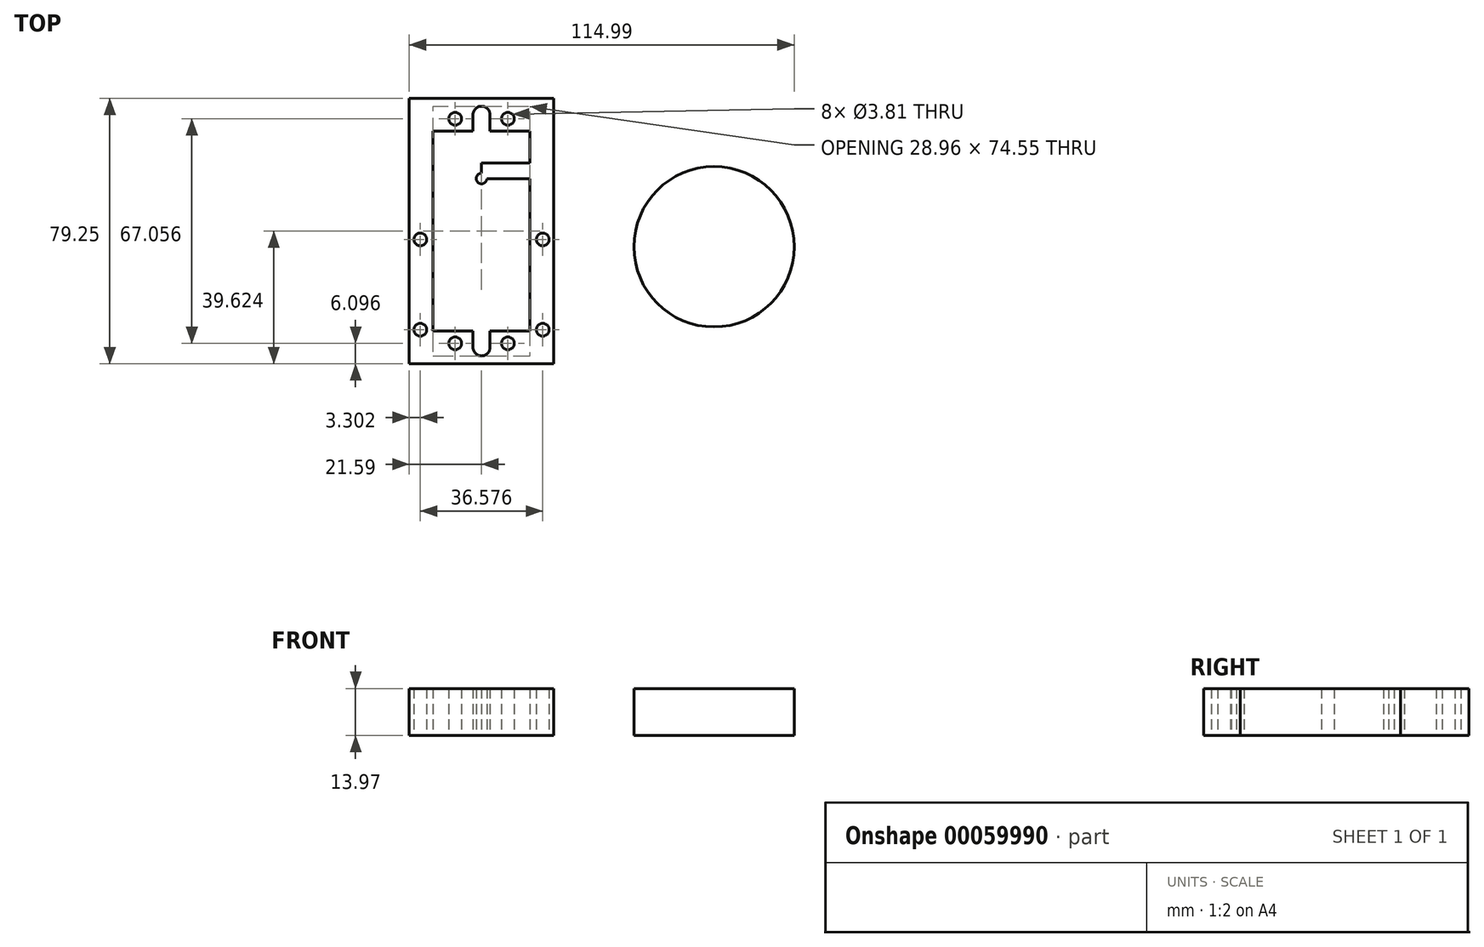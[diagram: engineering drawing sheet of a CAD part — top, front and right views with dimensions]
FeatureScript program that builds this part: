
annotation { "Feature Type Name" : "Feature", "Feature Type Description" : "" }
export const myFeature = defineFeature(function(context is Context, id is Id, definition is map)
    precondition{}
    {
        {
            var Q0;
            Q0=qCreatedBy(makeId("Top.planeOp"),FACE);
            var sketch = newSketch(context, id + "F0", { "sketchPlane" : qUnion([Q0])});
            skLineSegment(sketch, "E0.bottom", {"start": v(0, 0) * mm, "end": v(-43.18, 0) * mm});
            skLineSegment(sketch, "E0.top", {"start": v(0, 79.25) * mm, "end": v(-43.18, 79.25) * mm});
            skLineSegment(sketch, "E0.left", {"start": v(0, 0) * mm, "end": v(0, 79.25) * mm});
            skLineSegment(sketch, "E0.right", {"start": v(-43.18, 0) * mm, "end": v(-43.18, 79.25) * mm});
            skCircle(sketch, "E1", {"center": v(-29.46, 73.15) * mm, "radius": 1.9 * mm});
            skCircle(sketch, "E2", {"center": v(-29.46, 6.1) * mm, "radius": 1.9 * mm});
            skCircle(sketch, "E3", {"center": v(-39.88, 10.16) * mm, "radius": 1.9 * mm});
            skCircle(sketch, "E4", {"center": v(-39.88, 37.1) * mm, "radius": 1.9 * mm});
            skLineSegment(sketch, "E5", {"start": v(-21.59, 0) * mm, "end": v(-21.59, 79.25) * mm, "construction": true});
            skLineSegment(sketch, "E6.bottom", {"start": v(-24.13, 69.47) * mm, "end": v(-36.07, 69.47) * mm});
            skLineSegment(sketch, "E6.top", {"start": v(-24.13, 9.78) * mm, "end": v(-36.07, 9.78) * mm});
            skLineSegment(sketch, "E6.left", {"start": v(-21.59, 69.47) * mm, "end": v(-21.59, 9.78) * mm, "construction": true});
            skLineSegment(sketch, "E6.right", {"start": v(-36.07, 69.47) * mm, "end": v(-36.07, 9.78) * mm});
            skLineSegment(sketch, "E7", {"start": v(-21.59, 69.47) * mm, "end": v(-21.59, 79.25) * mm, "construction": true});
            skLineSegment(sketch, "E8", {"start": v(-21.59, 9.78) * mm, "end": v(-21.59, 0) * mm, "construction": true});
            skArc(sketch, "E9", {"start": v(-21.59, 76.9) * mm, "mid": v(-23.39, 76.15) * mm, "end": v(-24.13, 74.36) * mm});
            skLineSegment(sketch, "E10", {"start": v(-24.13, 74.36) * mm, "end": v(-24.13, 69.47) * mm});
            skLineSegment(sketch, "E11", {"start": v(-21.59, 71.82) * mm, "end": v(-21.59, 69.47) * mm});
            skArc(sketch, "E12", {"start": v(-24.13, 4.89) * mm, "mid": v(-23.39, 3.1) * mm, "end": v(-21.59, 2.35) * mm});
            skLineSegment(sketch, "E13", {"start": v(-24.13, 4.89) * mm, "end": v(-24.13, 9.78) * mm});
            skLineSegment(sketch, "E14", {"start": v(-21.59, 9.78) * mm, "end": v(-21.59, 7.43) * mm});
            skArc(sketch, "E15.MirrorCS", {"start": v(-21.59, 76.9) * mm, "mid": v(-19.8, 76.15) * mm, "end": v(-19.05, 74.36) * mm});
            skLineSegment(sketch, "E16.MirrorCS", {"start": v(-19.05, 74.36) * mm, "end": v(-19.05, 69.47) * mm});
            skLineSegment(sketch, "E17.MirrorCS", {"start": v(-19.05, 69.47) * mm, "end": v(-7.11, 69.47) * mm});
            skCircle(sketch, "E18.MirrorC", {"center": v(-13.72, 73.15) * mm, "radius": 1.9 * mm});
            skLineSegment(sketch, "E19.MirrorCS", {"start": v(-7.11, 69.47) * mm, "end": v(-7.11, 9.78) * mm});
            skCircle(sketch, "E20.MirrorC", {"center": v(-3.3, 37.1) * mm, "radius": 1.9 * mm});
            skCircle(sketch, "E21.MirrorC", {"center": v(-3.3, 10.16) * mm, "radius": 1.9 * mm});
            skCircle(sketch, "E22.MirrorC", {"center": v(-13.72, 6.1) * mm, "radius": 1.9 * mm});
            skLineSegment(sketch, "E23.MirrorCS", {"start": v(-19.05, 9.78) * mm, "end": v(-7.11, 9.78) * mm});
            skLineSegment(sketch, "E24.MirrorCS", {"start": v(-19.05, 4.89) * mm, "end": v(-19.05, 9.78) * mm});
            skArc(sketch, "E25.MirrorCS", {"start": v(-19.05, 4.89) * mm, "mid": v(-19.8, 3.1) * mm, "end": v(-21.59, 2.35) * mm});
            skCircle(sketch, "E26", {"center": v(-21.59, 55.3) * mm, "radius": 1.59 * mm});
            skLineSegment(sketch, "E27.bottom", {"start": v(-21.59, 55.3) * mm, "end": v(-7.11, 55.3) * mm});
            skLineSegment(sketch, "E27.top", {"start": v(-21.59, 59.91) * mm, "end": v(-7.11, 59.91) * mm});
            skLineSegment(sketch, "E27.left", {"start": v(-21.59, 55.3) * mm, "end": v(-21.59, 59.91) * mm});
            skLineSegment(sketch, "E27.right", {"start": v(-7.11, 55.3) * mm, "end": v(-7.11, 59.91) * mm});
            skSolve(sketch);
        }
        {
            var Q0;
            Q0=makeQuery(id+"F0.imprint","IMPRINT",FACE,{"disambiguationData":[TD([[makeQuery(id+"F0.imprint","IMPRINT",EDGE,{"derivedFrom":sQuery(id+"F0.wireOp",EDGE,"E0.bottom")}),-1.0]])]});
            var Q1;
            {var subQ1=sQuery(id+"F0.wireOp",EDGE,"E27.top");Q1=makeQuery(id+"F0.imprint","IMPRINT",FACE,{"disambiguationData":[TD([[makeQuery(id+"F0.imprint","IMPRINT",EDGE,{"derivedFrom":subQ1}),-1.0]])]});}
            var Q2;
            {var subQ0=sQuery(id+"F0.wireOp",EDGE,"E27.bottom");var subQ1=sQuery(id+"F0.wireOp",EDGE,"E26");var subQ2=makeQuery(id+"F0.imprint","INTERSECT",VERTEX,{"derivedFrom":[subQ1,subQ0]});Q2=makeQuery(id+"F0.imprint","IMPRINT",FACE,{"disambiguationData":[TD([[makeQuery(id+"F0.imprint","IMPRINT",EDGE,{"disambiguationData":[TD([[subQ2,-1.0]])],"derivedFrom":subQ1}),1.0]])]});}
            var Q3;
            {var subQ0=sQuery(id+"F0.wireOp",EDGE,"E27.bottom");var subQ1=sQuery(id+"F0.wireOp",EDGE,"E26");var subQ2=makeQuery(id+"F0.imprint","INTERSECT",VERTEX,{"derivedFrom":[subQ1,subQ0]});Q3=makeQuery(id+"F0.imprint","IMPRINT",FACE,{"disambiguationData":[TD([[makeQuery(id+"F0.imprint","IMPRINT",EDGE,{"disambiguationData":[TD([[subQ2,1.0]])],"derivedFrom":subQ1}),1.0]])]});}
            extrude(context, id + "F1", {"entities" : qUnion([Q0, Q1, Q2, Q3]), "depth" : 13.97 * mm});
        }
        {
            var Q0;
            Q0=qCreatedBy(makeId("Top.planeOp"),FACE);
            var sketch = newSketch(context, id + "F2", { "sketchPlane" : qUnion([Q0])});
            skCircle(sketch, "E28", {"center": v(47.87, 34.93) * mm, "radius": 23.94 * mm});
            skSolve(sketch);
        }
        {
            var Q0;
            Q0=makeQuery(id+"F2.imprint","IMPRINT",FACE,{"disambiguationData":[TD([[makeQuery(id+"F2.imprint","IMPRINT",EDGE,{"derivedFrom":sQuery(id+"F2.wireOp",EDGE,"E28")}),1.0]])]});
            extrude(context, id + "F3", {"entities" : qUnion([Q0]), "depth" : 13.97 * mm});
        }
    });
